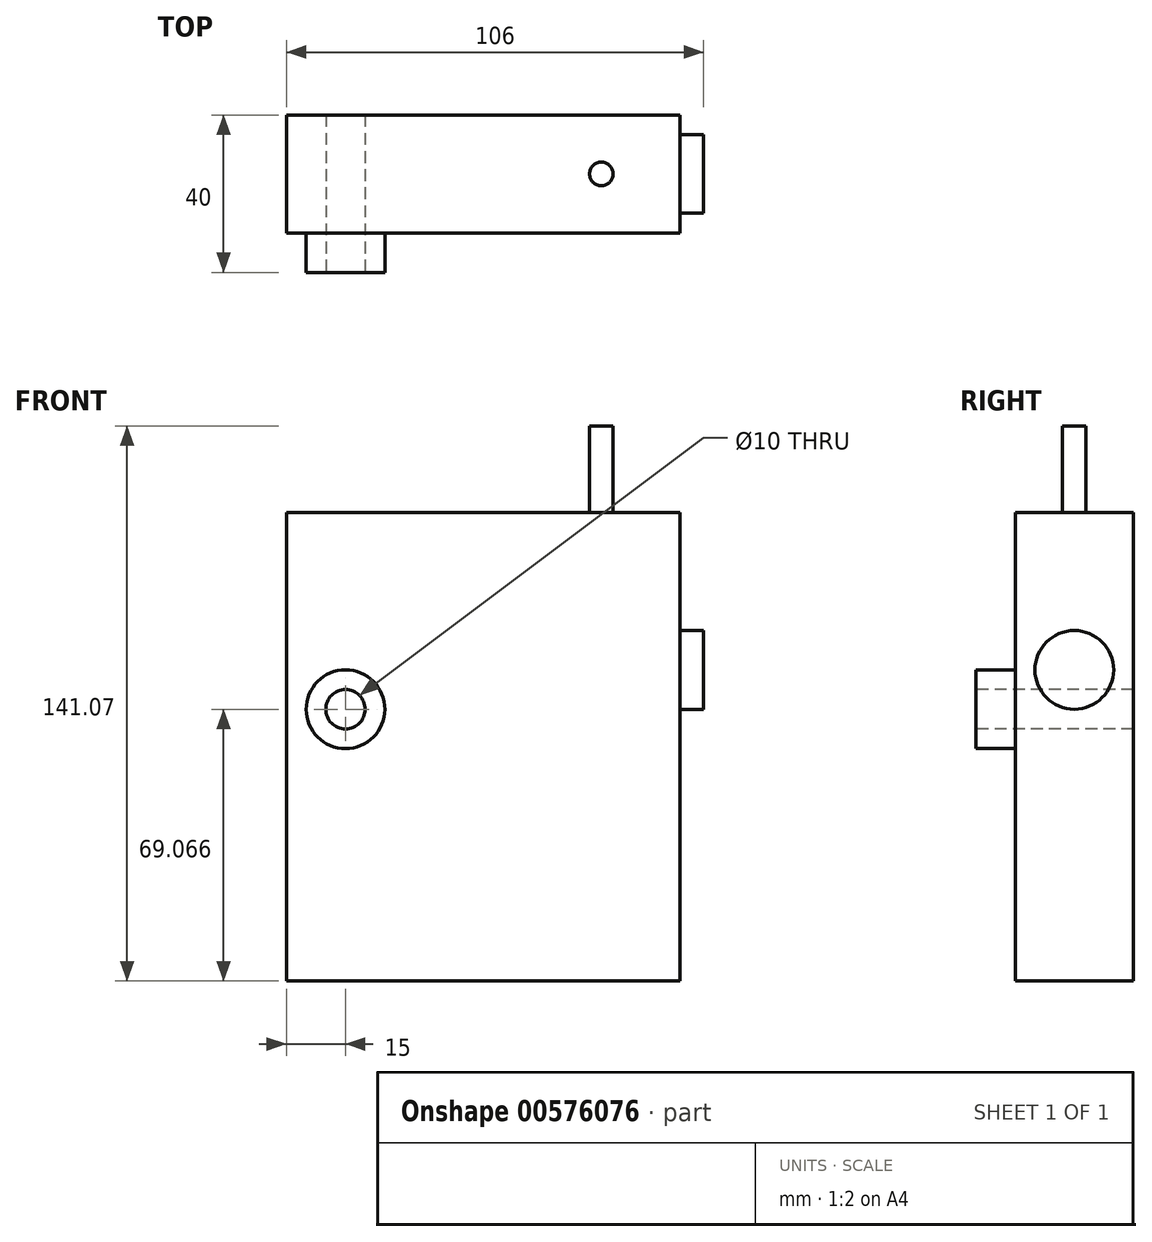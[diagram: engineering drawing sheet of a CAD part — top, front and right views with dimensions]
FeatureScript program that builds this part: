
annotation { "Feature Type Name" : "Feature", "Feature Type Description" : "" }
export const myFeature = defineFeature(function(context is Context, id is Id, definition is map)
    precondition{}
    {
        {
            var Q0;
            Q0=qCreatedBy(makeId("Front.planeOp"),FACE);
            var sketch = newSketch(context, id + "F0", { "sketchPlane" : qUnion([Q0])});
            skLineSegment(sketch, "E0.bottom", {"start": v(50, 55.9) * mm, "end": v(-50, 55.9) * mm});
            skLineSegment(sketch, "E0.top", {"start": v(50, -63.16) * mm, "end": v(-50, -63.16) * mm});
            skLineSegment(sketch, "E0.left", {"start": v(50, 55.9) * mm, "end": v(50, -63.16) * mm});
            skLineSegment(sketch, "E0.right", {"start": v(-50, 55.9) * mm, "end": v(-50, -63.16) * mm});
            skPoint(sketch, "E0.middle", {"position": v(0, -3.63) * mm});
            skSolve(sketch);
        }
        {
            var Q0;
            Q0=makeQuery(id+"F0.imprint","IMPRINT",FACE,{"disambiguationData":[TD([[makeQuery(id+"F0.imprint","IMPRINT",EDGE,{"derivedFrom":sQuery(id+"F0.wireOp",EDGE,"E0.bottom")}),1.0]])]});
            extrude(context, id + "F1", {"entities" : qUnion([Q0]), "endBound" : BoundingType.SYMMETRIC, "depth" : 30 * mm, "offsetDistance" : 25.4 * mm});
        }
        {
            var Q0;
            Q0=makeQuery(id+"F1.opExtrude","CAP_FACE",FACE,{"disambiguationData":[OSD([sQuery(id+"F0.wireOp",EDGE,"E0.bottom"),sQuery(id+"F0.wireOp",EDGE,"E0.top"),sQuery(id+"F0.wireOp",EDGE,"E0.left"),sQuery(id+"F0.wireOp",EDGE,"E0.right")])],"isStart":false});
            var sketch = newSketch(context, id + "F2", { "sketchPlane" : qUnion([Q0])});
            skCircle(sketch, "E1", {"center": v(-35, 5.9) * mm, "radius": 10 * mm});
            skSolve(sketch);
        }
        {
            var Q0;
            Q0=qSketchRegion(id+"F2",true);
            extrude(context, id + "F3", {"entities" : qUnion([Q0]), "operationType" : NewBodyOperationType.ADD, "depth" : 10 * mm, "offsetDistance" : 25.4 * mm});
        }
        {
            var Q0;
            Q0=makeQuery(id+"F1.opExtrude","SWEPT_FACE",FACE,{"disambiguationData":[OSD([sQuery(id+"F0.wireOp",EDGE,"E0.left")])]});
            var sketch = newSketch(context, id + "F4", { "sketchPlane" : qUnion([Q0])});
            skCircle(sketch, "E2", {"center": v(0, 15.9) * mm, "radius": 10 * mm});
            skSolve(sketch);
        }
        {
            var Q0;
            Q0=qSketchRegion(id+"F4",true);
            extrude(context, id + "F5", {"entities" : qUnion([Q0]), "operationType" : NewBodyOperationType.ADD, "depth" : 6 * mm, "offsetDistance" : 25 * mm});
        }
        {
            var Q0;
            Q0=makeQuery(id+"F1.opExtrude","SWEPT_FACE",FACE,{"disambiguationData":[OSD([sQuery(id+"F0.wireOp",EDGE,"E0.bottom")])]});
            var sketch = newSketch(context, id + "F6", { "sketchPlane" : qUnion([Q0])});
            skCircle(sketch, "E3", {"center": v(30, 0) * mm, "radius": 3 * mm});
            skSolve(sketch);
        }
        {
            var Q0;
            Q0=qSketchRegion(id+"F6",true);
            extrude(context, id + "F7", {"entities" : qUnion([Q0]), "operationType" : NewBodyOperationType.ADD, "depth" : 22 * mm, "offsetDistance" : 25 * mm});
        }
        {
            var Q0;
            Q0=makeQuery(id+"F3.opExtrude","CAP_FACE",FACE,{"disambiguationData":[OSD([sQuery(id+"F2.wireOp",EDGE,"E1")])],"isStart":false});
            var sketch = newSketch(context, id + "F8", { "sketchPlane" : qUnion([Q0])});
            skCircle(sketch, "E4", {"center": v(-35, 5.9) * mm, "radius": 5 * mm});
            skSolve(sketch);
        }
        {
            var Q0;
            Q0=qSketchRegion(id+"F8",true);
            extrude(context, id + "F9", {"entities" : qUnion([Q0]), "operationType" : NewBodyOperationType.REMOVE, "endBound" : BoundingType.THROUGH_ALL, "oppositeDirection" : true, "depth" : 25 * mm, "offsetDistance" : 25 * mm});
        }
    });
